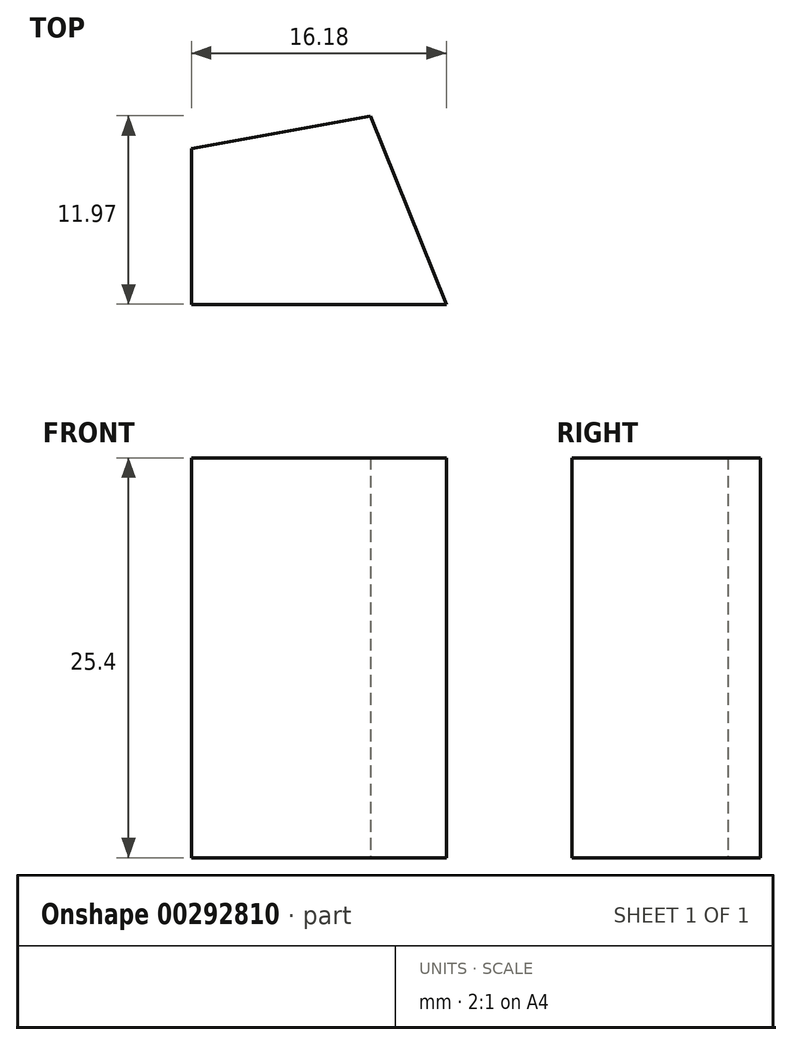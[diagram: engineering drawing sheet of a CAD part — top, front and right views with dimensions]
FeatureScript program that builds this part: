
annotation { "Feature Type Name" : "Feature", "Feature Type Description" : "" }
export const myFeature = defineFeature(function(context is Context, id is Id, definition is map)
    precondition{}
    {
        {
            var Q0;
            Q0=qCreatedBy(makeId("Top.planeOp"),FACE);
            var sketch = newSketch(context, id + "F0", { "sketchPlane" : qUnion([Q0])});
            skLineSegment(sketch, "E0", {"start": v(67.7, 32.45) * mm, "end": v(56.27, 32.45) * mm});
            skLineSegment(sketch, "E1", {"start": v(56.27, 32.45) * mm, "end": v(56.27, 26.58) * mm});
            skLineSegment(sketch, "E2", {"start": v(56.27, 26.58) * mm, "end": v(88.1, 26.58) * mm});
            skLineSegment(sketch, "E3", {"start": v(88.1, 26.58) * mm, "end": v(88.1, 33.38) * mm});
            skLineSegment(sketch, "E4", {"start": v(54.41, 53.48) * mm, "end": v(56.88, 53.48) * mm});
            skLineSegment(sketch, "E5", {"start": v(105.68, 30.76) * mm, "end": v(116.5, 30.76) * mm});
            skLineSegment(sketch, "E6", {"start": v(116.5, 30.76) * mm, "end": v(116.5, 55.43) * mm});
            skLineSegment(sketch, "E7", {"start": v(116.5, 55.43) * mm, "end": v(102.98, 55.43) * mm});
            skLineSegment(sketch, "E8", {"start": v(106.09, 22.1) * mm, "end": v(106.09, 12.23) * mm});
            skLineSegment(sketch, "E9", {"start": v(106.09, 12.23) * mm, "end": v(122.27, 12.23) * mm});
            skLineSegment(sketch, "E10", {"start": v(122.27, 12.23) * mm, "end": v(117.44, 24.2) * mm});
            skLineSegment(sketch, "E11", {"start": v(117.44, 24.2) * mm, "end": v(106.09, 22.1) * mm});
            skPoint(sketch, "E12.end.orphan", {"position": v(19.17, 53.48) * mm});
            skPoint(sketch, "E13.end.orphan", {"position": v(94.6, 53.48) * mm});
            skSolve(sketch);
        }
        {
            var Q0;
            Q0 = qSketchRegion(id + "F0", true);
            extrude(context, id + "F1", {"entities" : qUnion([Q0]), "depth" : 25.4 * mm});
        }
        {
            var Q0;
            Q0 = qSketchRegion(id + "F0", true);
            extrude(context, id + "F2", {"entities" : qUnion([Q0]), "depth" : 25.4 * mm});
        }
    });
